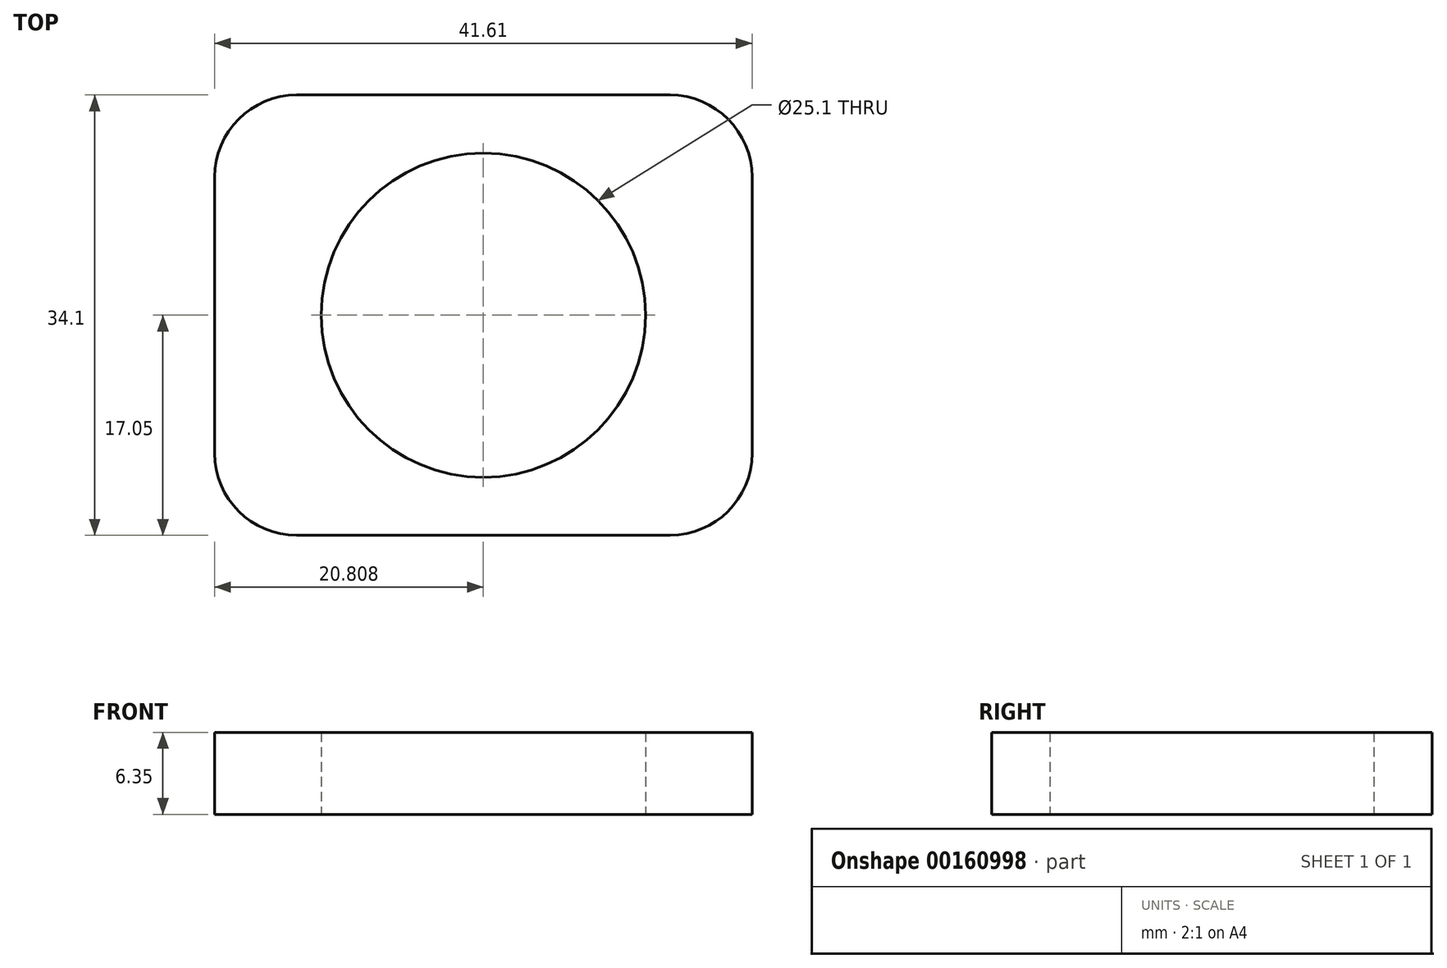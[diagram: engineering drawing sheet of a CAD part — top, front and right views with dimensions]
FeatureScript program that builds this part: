
annotation { "Feature Type Name" : "Feature", "Feature Type Description" : "" }
export const myFeature = defineFeature(function(context is Context, id is Id, definition is map)
    precondition{}
    {
        {
            var Q0;
            Q0=qCreatedBy(makeId("Top.planeOp"),FACE);
            var sketch = newSketch(context, id + "F0", { "sketchPlane" : qUnion([Q0])});
            skLineSegment(sketch, "E0.bottom", {"start": v(-47.9, 64.25) * mm, "end": v(-19, 64.25) * mm});
            skLineSegment(sketch, "E0.top", {"start": v(-47.9, 30.15) * mm, "end": v(-19, 30.15) * mm});
            skLineSegment(sketch, "E0.left", {"start": v(-54.26, 57.9) * mm, "end": v(-54.26, 36.5) * mm});
            skLineSegment(sketch, "E0.right", {"start": v(-12.65, 57.9) * mm, "end": v(-12.65, 36.5) * mm});
            skPoint(sketch, "E1.visualSharp", {"position": v(-54.26, 64.25) * mm});
            skArc(sketch, "E1.filletArc", {"start": v(-47.9, 64.25) * mm, "mid": v(-52.4, 62.39) * mm, "end": v(-54.26, 57.9) * mm});
            skPoint(sketch, "E2.visualSharp", {"position": v(-12.65, 64.25) * mm});
            skArc(sketch, "E2.filletArc", {"start": v(-12.65, 57.9) * mm, "mid": v(-14.5, 62.39) * mm, "end": v(-19, 64.25) * mm});
            skPoint(sketch, "E3.visualSharp", {"position": v(-12.65, 30.15) * mm});
            skArc(sketch, "E3.filletArc", {"start": v(-19, 30.15) * mm, "mid": v(-14.5, 32.01) * mm, "end": v(-12.65, 36.5) * mm});
            skPoint(sketch, "E4.visualSharp", {"position": v(-54.26, 30.15) * mm});
            skArc(sketch, "E4.filletArc", {"start": v(-54.26, 36.5) * mm, "mid": v(-52.4, 32.01) * mm, "end": v(-47.9, 30.15) * mm});
            skLineSegment(sketch, "E5", {"start": v(-33.45, 64.25) * mm, "end": v(-33.45, 30.15) * mm});
            skCircle(sketch, "E6", {"center": v(-33.45, 47.2) * mm, "radius": 12.55 * mm});
            skSolve(sketch);
        }
        {
            var Q0;
            Q0=makeQuery(id+"F0.imprint","IMPRINT",FACE,{"disambiguationData":[TD([[makeQuery(id+"F0.imprint","IMPRINT",EDGE,{"derivedFrom":sQuery(id+"F0.wireOp",EDGE,"E0.left")}),1.0]])]});
            var Q1;
            Q1=makeQuery(id+"F0.imprint","IMPRINT",FACE,{"disambiguationData":[TD([[makeQuery(id+"F0.imprint","IMPRINT",EDGE,{"derivedFrom":sQuery(id+"F0.wireOp",EDGE,"E0.right")}),-1.0]])]});
            extrude(context, id + "F1", {"entities" : qUnion([Q0, Q1]), "depth" : 6.35 * mm});
        }
    });
